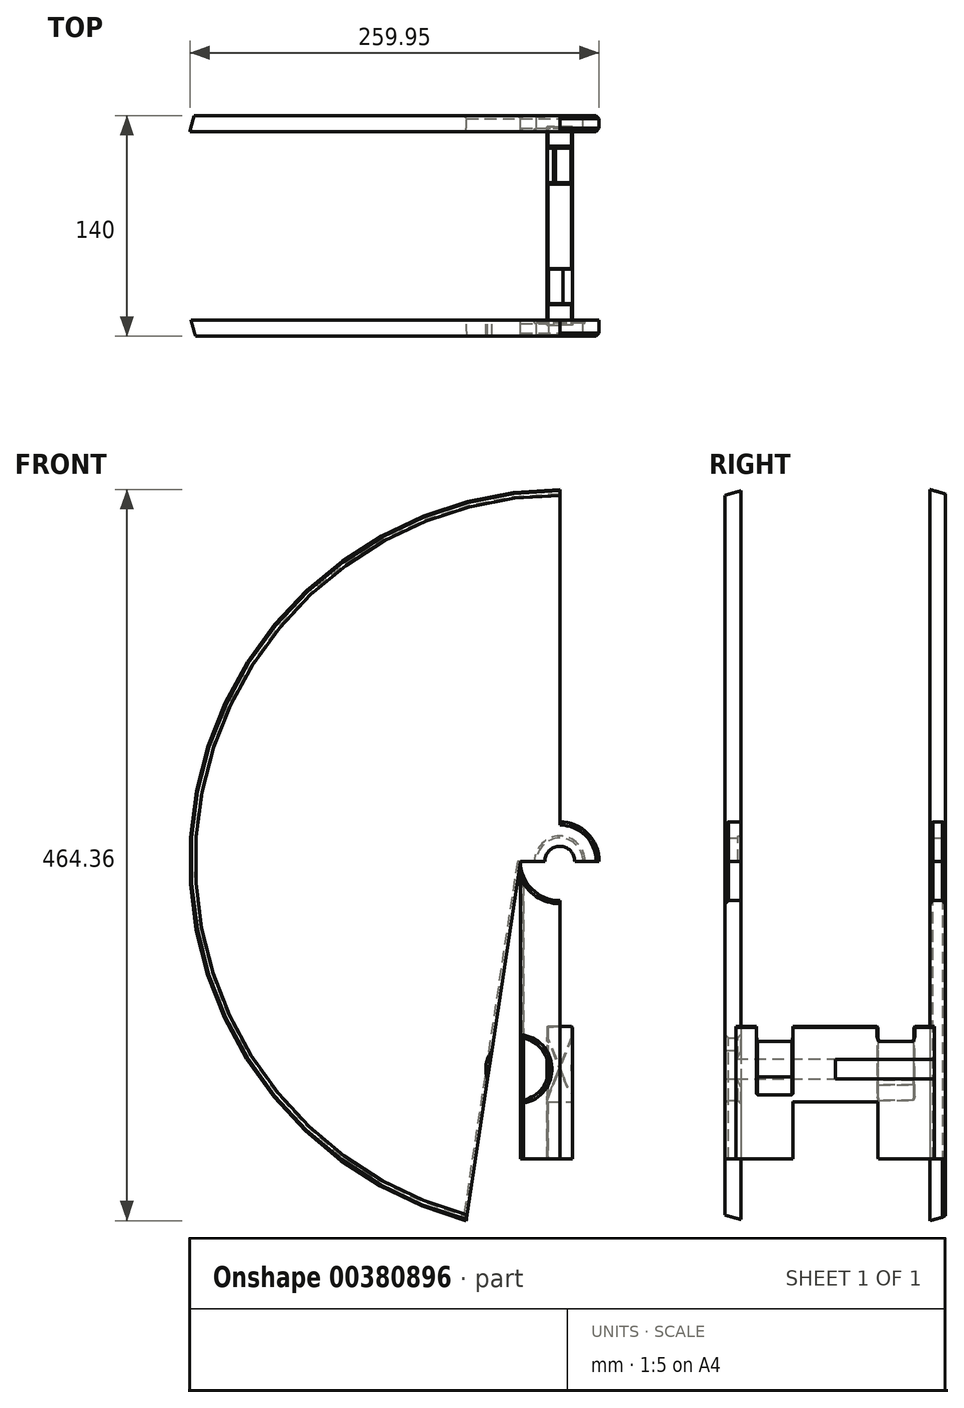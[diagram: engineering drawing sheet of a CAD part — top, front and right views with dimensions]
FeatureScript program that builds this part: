
annotation { "Feature Type Name" : "Feature", "Feature Type Description" : "" }
export const myFeature = defineFeature(function(context is Context, id is Id, definition is map)
    precondition{}
    {
        {
            var Q0;
            Q0=qCreatedBy(makeId("Right.planeOp"),FACE);
            var sketch = newSketch(context, id + "F0", { "sketchPlane" : qUnion([Q0])});
            skCircle(sketch, "E0", {"center": v(0, 0) * mm, "radius": 243.58 * mm});
            skLineSegment(sketch, "E1", {"start": v(1.44, 243.58) * mm, "end": v(1.44, -243.58) * mm});
            skCircle(sketch, "E2", {"center": v(0, 0) * mm, "radius": 251.5 * mm});
            skLineSegment(sketch, "E3", {"start": v(1.44, 243.58) * mm, "end": v(1.44, -357.35) * mm});
            skLineSegment(sketch, "E4", {"start": v(1.44, -357.35) * mm, "end": v(1.44, 517.62) * mm});
            skSolve(sketch);
        }
        {
            var Q0;
            Q0=qCreatedBy(makeId("Top.planeOp"),FACE);
            var sketch = newSketch(context, id + "F1", { "sketchPlane" : qUnion([Q0])});
            skCircle(sketch, "E5", {"center": v(0, 0) * mm, "radius": 243.58 * mm});
            skCircle(sketch, "E6", {"center": v(0, 0) * mm, "radius": 251.5 * mm});
            skSolve(sketch);
        }
        {
            var Q0;
            Q0=makeQuery(id+"F1.imprint","IMPRINT",FACE,{"disambiguationData":[TD([[makeQuery(id+"F1.imprint","IMPRINT",EDGE,{"derivedFrom":sQuery(id+"F1.wireOp",EDGE,"E5")}),1.0]])]});
            var sketch = newSketch(context, id + "F2", { "sketchPlane" : qUnion([Q0])});
            skCircle(sketch, "E7", {"center": v(0, 0) * mm, "radius": 50 * mm});
            skCircle(sketch, "E8", {"center": v(0, 0) * mm, "radius": 57.5 * mm});
            skSolve(sketch);
        }
        {
            var Q0;
            Q0=qCreatedBy(makeId("Front.planeOp"),FACE);
            var sketch = newSketch(context, id + "F3", { "sketchPlane" : qUnion([Q0])});
            skLineSegment(sketch, "E9.bottom", {"start": v(59.85, -25) * mm, "end": v(-59.85, -25) * mm});
            skLineSegment(sketch, "E9.top", {"start": v(59.85, 25) * mm, "end": v(-59.85, 25) * mm});
            skLineSegment(sketch, "E9.left", {"start": v(59.85, -25) * mm, "end": v(59.85, 25) * mm});
            skLineSegment(sketch, "E9.right", {"start": v(-59.85, -25) * mm, "end": v(-59.85, 25) * mm});
            skPoint(sketch, "E9.middle", {"position": v(0, 0) * mm});
            skCircle(sketch, "E10", {"center": v(0, 0) * mm, "radius": 14.75 * mm});
            skCircle(sketch, "E11", {"center": v(0, 0) * mm, "radius": 16 * mm});
            skCircle(sketch, "E12", {"center": v(0, 0) * mm, "radius": 9.5 * mm});
            skSolve(sketch);
        }
        {
            var Q0;
            Q0=qCreatedBy(makeId("Front.planeOp"),FACE);
            var sketch = newSketch(context, id + "F4", { "sketchPlane" : qUnion([Q0])});
            skCircle(sketch, "E13", {"center": v(0, 0) * mm, "radius": 25 * mm});
            skCircle(sketch, "E14", {"center": v(-1.44, -4.53) * mm, "radius": 243.58 * mm});
            skLineSegment(sketch, "E15", {"start": v(0, 239.04) * mm, "end": v(0, -248.1) * mm});
            skCircle(sketch, "E16", {"center": v(-1.44, -4.53) * mm, "radius": 251.5 * mm});
            skLineSegment(sketch, "E17", {"start": v(-25, 0) * mm, "end": v(-61.37, -240.62) * mm});
            skLineSegment(sketch, "E18.MirrorCS", {"start": v(25, 0) * mm, "end": v(61.37, -240.62) * mm});
            skLineSegment(sketch, "E19.bottom", {"start": v(-25, 0) * mm, "end": v(25, 0) * mm});
            skLineSegment(sketch, "E19.top", {"start": v(-25, -189.15) * mm, "end": v(25, -189.15) * mm});
            skLineSegment(sketch, "E19.left", {"start": v(-25, 0) * mm, "end": v(-25, -189.15) * mm});
            skLineSegment(sketch, "E19.right", {"start": v(25, 0) * mm, "end": v(25, -189.15) * mm});
            skSolve(sketch);
        }
        {
            var Q0;
            {var subQ0=sQuery(id+"F4.wireOp",EDGE,"E13");var subQ1=makeQuery(id+"F4.imprint","INTERSECT",VERTEX,{"derivedFrom":[subQ0,sQuery(id+"F4.wireOp",EDGE,"E17")]});Q0=makeQuery(id+"F4.imprint","IMPRINT",FACE,{"disambiguationData":[TD([[makeQuery(id+"F4.imprint","IMPRINT",EDGE,{"disambiguationData":[TD([[subQ1,1.0]])],"derivedFrom":subQ0}),1.0]])]});}
            var Q1;
            {var subQ0=sQuery(id+"F4.wireOp",EDGE,"E13");var subQ1=makeQuery(id+"F4.imprint","INTERSECT",VERTEX,{"derivedFrom":[subQ0,sQuery(id+"F4.wireOp",EDGE,"E18.MirrorCS")]});Q1=makeQuery(id+"F4.imprint","IMPRINT",FACE,{"disambiguationData":[TD([[makeQuery(id+"F4.imprint","IMPRINT",EDGE,{"disambiguationData":[TD([[subQ1,-1.0]])],"derivedFrom":subQ0}),1.0]])]});}
            var Q2;
            {var subQ0=sQuery(id+"F4.wireOp",EDGE,"E15");var subQ1=sQuery(id+"F4.wireOp",EDGE,"E13");var subQ2=makeQuery(id+"F4.imprint","INTERSECT",VERTEX,{"disambiguationData":[OD(1.0)],"derivedFrom":[subQ1,subQ0]});Q2=makeQuery(id+"F4.imprint","IMPRINT",FACE,{"disambiguationData":[TD([[makeQuery(id+"F4.imprint","IMPRINT",EDGE,{"disambiguationData":[TD([[subQ2,-1.0]])],"derivedFrom":subQ1}),-1.0]])]});}
            var Q3;
            {var subQ0=sQuery(id+"F4.wireOp",EDGE,"E19.left");Q3=makeQuery(id+"F4.imprint","IMPRINT",FACE,{"disambiguationData":[TD([[makeQuery(id+"F4.imprint","IMPRINT",EDGE,{"derivedFrom":subQ0}),1.0]])]});}
            var Q4;
            {var subQ0=sQuery(id+"F4.wireOp",EDGE,"E15");var subQ1=sQuery(id+"F4.wireOp",EDGE,"E13");var subQ2=makeQuery(id+"F4.imprint","INTERSECT",VERTEX,{"disambiguationData":[OD(1.0)],"derivedFrom":[subQ1,subQ0]});Q4=makeQuery(id+"F4.imprint","IMPRINT",FACE,{"disambiguationData":[TD([[makeQuery(id+"F4.imprint","IMPRINT",EDGE,{"disambiguationData":[TD([[subQ2,-1.0]])],"derivedFrom":subQ1}),1.0]])]});}
            var Q5;
            {var subQ1=sQuery(id+"F4.wireOp",EDGE,"E13");var subQ3=sQuery(id+"F4.wireOp",EDGE,"E15");var subQ4=makeQuery(id+"F4.imprint","INTERSECT",VERTEX,{"disambiguationData":[OD(1.0)],"derivedFrom":[subQ1,subQ3]});Q5=makeQuery(id+"F4.imprint","IMPRINT",FACE,{"disambiguationData":[TD([[makeQuery(id+"F4.imprint","IMPRINT",EDGE,{"disambiguationData":[TD([[subQ4,1.0]])],"derivedFrom":subQ3}),-1.0]])]});}
            extrude(context, id + "F5", {"entities" : qUnion([Q0, Q1, Q2, Q3, Q4, Q5]), "endBound" : BoundingType.SYMMETRIC, "depth" : 140 * mm, "hasSecondDirection" : true, "secondDirectionOppositeDirection" : true, "secondDirectionDepth" : 71 * mm});
        }
        {
            var Q0;
            {var subQ5=sQuery(id+"F4.wireOp",EDGE,"E13");var subQ6=makeQuery(id+"F4.imprint","INTERSECT",VERTEX,{"derivedFrom":[subQ5,sQuery(id+"F4.wireOp",EDGE,"E18.MirrorCS")]});Q0=makeQuery(id+"F4.imprint","IMPRINT",FACE,{"disambiguationData":[TD([[makeQuery(id+"F4.imprint","IMPRINT",EDGE,{"disambiguationData":[TD([[subQ6,-1.0]])],"derivedFrom":subQ5}),1.0]])]});}
            var Q1;
            {var subQ1=sQuery(id+"F4.wireOp",EDGE,"E13");var subQ3=sQuery(id+"F4.wireOp",EDGE,"E15");var subQ4=makeQuery(id+"F4.imprint","INTERSECT",VERTEX,{"disambiguationData":[OD(0.0)],"derivedFrom":[subQ1,subQ3]});Q1=makeQuery(id+"F4.imprint","IMPRINT",FACE,{"disambiguationData":[TD([[makeQuery(id+"F4.imprint","IMPRINT",EDGE,{"disambiguationData":[TD([[subQ4,-1.0]])],"derivedFrom":subQ3}),-1.0]])]});}
            var Q2;
            {var subQ1=sQuery(id+"F4.wireOp",EDGE,"E13");var subQ3=sQuery(id+"F4.wireOp",EDGE,"E15");var subQ4=makeQuery(id+"F4.imprint","INTERSECT",VERTEX,{"disambiguationData":[OD(1.0)],"derivedFrom":[subQ1,subQ3]});Q2=makeQuery(id+"F4.imprint","IMPRINT",FACE,{"disambiguationData":[TD([[makeQuery(id+"F4.imprint","IMPRINT",EDGE,{"disambiguationData":[TD([[subQ4,1.0]])],"derivedFrom":subQ3}),-1.0]])]});}
            var Q3;
            {var subQ0=sQuery(id+"F4.wireOp",EDGE,"E15");var subQ1=sQuery(id+"F4.wireOp",EDGE,"E13");var subQ2=makeQuery(id+"F4.imprint","INTERSECT",VERTEX,{"disambiguationData":[OD(1.0)],"derivedFrom":[subQ1,subQ0]});Q3=makeQuery(id+"F4.imprint","IMPRINT",FACE,{"disambiguationData":[TD([[makeQuery(id+"F4.imprint","IMPRINT",EDGE,{"disambiguationData":[TD([[subQ2,-1.0]])],"derivedFrom":subQ1}),1.0]])]});}
            var Q4;
            {var subQ0=sQuery(id+"F4.wireOp",EDGE,"E15");var subQ1=sQuery(id+"F4.wireOp",EDGE,"E13");var subQ2=makeQuery(id+"F4.imprint","INTERSECT",VERTEX,{"disambiguationData":[OD(1.0)],"derivedFrom":[subQ1,subQ0]});Q4=makeQuery(id+"F4.imprint","IMPRINT",FACE,{"disambiguationData":[TD([[makeQuery(id+"F4.imprint","IMPRINT",EDGE,{"disambiguationData":[TD([[subQ2,-1.0]])],"derivedFrom":subQ1}),-1.0]])]});}
            var Q5;
            {var subQ0=sQuery(id+"F4.wireOp",EDGE,"E19.left");Q5=makeQuery(id+"F4.imprint","IMPRINT",FACE,{"disambiguationData":[TD([[makeQuery(id+"F4.imprint","IMPRINT",EDGE,{"derivedFrom":subQ0}),1.0]])]});}
            extrude(context, id + "F6", {"entities" : qUnion([Q0, Q1, Q2, Q3, Q4, Q5]), "operationType" : NewBodyOperationType.REMOVE, "endBound" : BoundingType.SYMMETRIC, "oppositeDirection" : true, "depth" : 120 * mm});
        }
        {
            var Q0;
            {var subQ0=sQuery(id+"F0.wireOp",EDGE,"E4");var subQ1=sQuery(id+"F0.wireOp",EDGE,"E0");var subQ2=makeQuery(id+"F0.imprint","INTERSECT",VERTEX,{"disambiguationData":[OD(0.0)],"derivedFrom":[subQ1,subQ0]});Q0=makeQuery(id+"F0.imprint","IMPRINT",FACE,{"disambiguationData":[TD([[makeQuery(id+"F0.imprint","IMPRINT",EDGE,{"disambiguationData":[TD([[subQ2,1.0]])],"derivedFrom":subQ1}),1.0]])]});}
            var Q1;
            Q1=sQuery(id+"F0.wireOp",EDGE,"E4");
            revolve(context, id + "F7", {"operationType" : NewBodyOperationType.INTERSECT, "entities" : qUnion([Q0]), "axis" : qUnion([Q1]), "revolveType" : RevolveType.FULL});
        }
        {
            var Q0;
            Q0=makeQuery(id+"F3.imprint","IMPRINT",FACE,{"disambiguationData":[TD([[makeQuery(id+"F3.imprint","IMPRINT",EDGE,{"derivedFrom":sQuery(id+"F3.wireOp",EDGE,"E10")}),1.0]])]});
            var Q1;
            Q1=makeQuery(id+"F3.imprint","IMPRINT",FACE,{"disambiguationData":[TD([[makeQuery(id+"F3.imprint","IMPRINT",EDGE,{"derivedFrom":sQuery(id+"F3.wireOp",EDGE,"E10")}),-1.0]])]});
            var Q2;
            Q2=sQuery(id+"F4.wireOp",EDGE,"E13");
            extrude(context, id + "F8", {"entities" : qUnion([Q0, Q1]), "operationType" : NewBodyOperationType.REMOVE, "surfaceEntities" : qUnion([Q2]), "endBound" : BoundingType.SYMMETRIC, "depth" : 123.5 * mm});
        }
        {
            var Q0;
            Q0=makeQuery(id+"F3.imprint","IMPRINT",FACE,{"disambiguationData":[TD([[makeQuery(id+"F3.imprint","IMPRINT",EDGE,{"derivedFrom":sQuery(id+"F3.wireOp",EDGE,"E10")}),1.0]])]});
            extrude(context, id + "F9", {"entities" : qUnion([Q0]), "operationType" : NewBodyOperationType.REMOVE, "endBound" : BoundingType.SYMMETRIC, "depth" : 139 * mm});
        }
        {
            var Q0;
            Q0=qCreatedBy(makeId("Front.planeOp"),FACE);
            var sketch = newSketch(context, id + "F10", { "sketchPlane" : qUnion([Q0])});
            skLineSegment(sketch, "E20.bottom", {"start": v(-62.5, 105) * mm, "end": v(62.5, 105) * mm, "construction": true});
            skLineSegment(sketch, "E20.top", {"start": v(-62.5, -105) * mm, "end": v(62.5, -105) * mm, "construction": true});
            skLineSegment(sketch, "E20.left", {"start": v(-62.5, 105) * mm, "end": v(-62.5, -105) * mm, "construction": true});
            skLineSegment(sketch, "E20.right", {"start": v(62.5, 105) * mm, "end": v(62.5, -105) * mm, "construction": true});
            skPoint(sketch, "E20.middle", {"position": v(0, 0) * mm});
            skLineSegment(sketch, "E21", {"start": v(0, 0) * mm, "end": v(0, -232.3) * mm, "construction": true});
            skPoint(sketch, "E22.firstSnap0", {"position": v(0, -105) * mm});
            skLineSegment(sketch, "E22.bottom", {"start": v(0, -105) * mm, "end": v(-8.15, -105) * mm});
            skLineSegment(sketch, "E22.top", {"start": v(0, -232.3) * mm, "end": v(-8.15, -232.3) * mm});
            skLineSegment(sketch, "E22.left", {"start": v(0, -105) * mm, "end": v(0, -232.3) * mm});
            skLineSegment(sketch, "E22.right", {"start": v(-8.15, -105) * mm, "end": v(-8.15, -232.3) * mm});
            skLineSegment(sketch, "E23.bottom", {"start": v(0, -105) * mm, "end": v(8.15, -105) * mm});
            skLineSegment(sketch, "E23.top", {"start": v(0, -232.3) * mm, "end": v(8.15, -232.3) * mm});
            skLineSegment(sketch, "E23.right", {"start": v(8.15, -105) * mm, "end": v(8.15, -232.3) * mm});
            skSolve(sketch);
        }
        {
            var Q0;
            Q0=makeQuery(id+"F3.imprint","IMPRINT",FACE,{"disambiguationData":[TD([[makeQuery(id+"F3.imprint","IMPRINT",EDGE,{"derivedFrom":sQuery(id+"F3.wireOp",EDGE,"E12")}),1.0]])]});
            var Q1;
            Q1=sQuery(id+"F3.wireOp",EDGE,"E12");
            extrude(context, id + "F11", {"entities" : qUnion([Q0]), "operationType" : NewBodyOperationType.REMOVE, "surfaceEntities" : qUnion([Q1]), "endBound" : BoundingType.SYMMETRIC, "oppositeDirection" : true, "depth" : 200 * mm});
        }
        {
            var Q0;
            Q0=makeQuery(id+"F10.imprint","IMPRINT",FACE,{"disambiguationData":[TD([[makeQuery(id+"F10.imprint","IMPRINT",EDGE,{"derivedFrom":sQuery(id+"F10.wireOp",EDGE,"E23.bottom")}),-1.0]])]});
            var Q1;
            Q1=makeQuery(id+"F10.imprint","IMPRINT",FACE,{"disambiguationData":[TD([[makeQuery(id+"F10.imprint","IMPRINT",EDGE,{"derivedFrom":sQuery(id+"F10.wireOp",EDGE,"E22.bottom")}),1.0]])]});
            extrude(context, id + "F12", {"entities" : qUnion([Q0, Q1]), "operationType" : NewBodyOperationType.REMOVE, "endBound" : BoundingType.SYMMETRIC, "oppositeDirection" : true, "depth" : 126 * mm});
        }
        {
            var Q0;
            Q0=qCreatedBy(makeId("Front.planeOp"),FACE);
            var sketch = newSketch(context, id + "F13", { "sketchPlane" : qUnion([Q0])});
            skLineSegment(sketch, "E24.bottom", {"start": v(-62.5, 105) * mm, "end": v(62.5, 105) * mm, "construction": true});
            skLineSegment(sketch, "E24.top", {"start": v(-62.5, -105) * mm, "end": v(62.5, -105) * mm, "construction": true});
            skLineSegment(sketch, "E24.left", {"start": v(-62.5, 105) * mm, "end": v(-62.5, -105) * mm, "construction": true});
            skLineSegment(sketch, "E24.right", {"start": v(62.5, 105) * mm, "end": v(62.5, -105) * mm, "construction": true});
            skPoint(sketch, "E24.middle", {"position": v(0, 0) * mm});
            skLineSegment(sketch, "E25", {"start": v(0, 0) * mm, "end": v(0, -189) * mm, "construction": true});
            skPoint(sketch, "E26.firstSnap0", {"position": v(0, -105) * mm});
            skLineSegment(sketch, "E26.bottom", {"start": v(0, -105) * mm, "end": v(-8, -105) * mm});
            skLineSegment(sketch, "E26.top", {"start": v(0, -189) * mm, "end": v(-8, -189) * mm});
            skLineSegment(sketch, "E26.left", {"start": v(0, -105) * mm, "end": v(0, -189) * mm});
            skLineSegment(sketch, "E26.right", {"start": v(-8, -105) * mm, "end": v(-8, -189) * mm});
            skLineSegment(sketch, "E27.bottom", {"start": v(0, -105) * mm, "end": v(8, -105) * mm});
            skLineSegment(sketch, "E27.top", {"start": v(0, -189) * mm, "end": v(8, -189) * mm});
            skLineSegment(sketch, "E27.right", {"start": v(8, -105) * mm, "end": v(8, -189) * mm});
            skLineSegment(sketch, "E28", {"start": v(-63.01, -125.52) * mm, "end": v(62.14, -125.52) * mm, "construction": true});
            skLineSegment(sketch, "E29.bottom", {"start": v(-56.15, -105) * mm, "end": v(-48.17, -105) * mm});
            skSolve(sketch);
        }
        {
            var Q0;
            Q0=qCreatedBy(makeId("Front.planeOp"),FACE);
            var sketch = newSketch(context, id + "F14", { "sketchPlane" : qUnion([Q0])});
            skLineSegment(sketch, "E30", {"start": v(-75.64, -132) * mm, "end": v(82.36, -132) * mm, "construction": true});
            skCircle(sketch, "E31", {"center": v(-26.97, -132) * mm, "radius": 20 * mm});
            skCircle(sketch, "E32", {"center": v(27.03, -132) * mm, "radius": 20 * mm});
            skLineSegment(sketch, "E33", {"start": v(0, -132) * mm, "end": v(0, 0) * mm, "construction": true});
            skSolve(sketch);
        }
        {
            var Q0;
            Q0=makeQuery(id+"F13.imprint","IMPRINT",FACE,{"disambiguationData":[TD([[makeQuery(id+"F13.imprint","IMPRINT",EDGE,{"derivedFrom":sQuery(id+"F13.wireOp",EDGE,"E26.bottom")}),1.0]])]});
            var Q1;
            Q1=makeQuery(id+"F13.imprint","IMPRINT",FACE,{"disambiguationData":[TD([[makeQuery(id+"F13.imprint","IMPRINT",EDGE,{"derivedFrom":sQuery(id+"F13.wireOp",EDGE,"E27.bottom")}),-1.0]])]});
            extrude(context, id + "F15", {"entities" : qUnion([Q0, Q1]), "endBound" : BoundingType.SYMMETRIC, "depth" : 126 * mm});
        }
        {
            var Q0;
            Q0=makeQuery(id+"F14.imprint","IMPRINT",FACE,{"disambiguationData":[TD([[makeQuery(id+"F14.imprint","IMPRINT",EDGE,{"derivedFrom":sQuery(id+"F14.wireOp",EDGE,"E32")}),1.0]])]});
            extrude(context, id + "F16", {"entities" : qUnion([Q0]), "operationType" : NewBodyOperationType.REMOVE, "oppositeDirection" : true, "depth" : 125.4 * mm});
        }
        {
            var Q0;
            Q0=makeQuery(id+"F14.imprint","IMPRINT",FACE,{"disambiguationData":[TD([[makeQuery(id+"F14.imprint","IMPRINT",EDGE,{"derivedFrom":sQuery(id+"F14.wireOp",EDGE,"E31")}),1.0]])]});
            extrude(context, id + "F17", {"entities" : qUnion([Q0]), "operationType" : NewBodyOperationType.REMOVE, "depth" : 97.5 * mm});
        }
        {
            var Q0;
            Q0=qCreatedBy(makeId("Front.planeOp"),FACE);
            var sketch = newSketch(context, id + "F18", { "sketchPlane" : qUnion([Q0])});
            skCircle(sketch, "E34", {"center": v(0, 0) * mm, "radius": 242.5 * mm});
            skSolve(sketch);
        }
        {
            var Q0;
            Q0=makeQuery(id+"F14.imprint","IMPRINT",FACE,{"disambiguationData":[TD([[makeQuery(id+"F14.imprint","IMPRINT",EDGE,{"derivedFrom":sQuery(id+"F14.wireOp",EDGE,"E31")}),1.0]])]});
            extrude(context, id + "F19", {"entities" : qUnion([Q0]), "operationType" : NewBodyOperationType.REMOVE, "depth" : 159.82 * mm, "hasSecondDirection" : true, "secondDirectionOppositeDirection" : false, "secondDirectionDepth" : 5 * mm});
        }
        {
            var Q0;
            Q0=makeQuery(id+"F14.imprint","IMPRINT",FACE,{"disambiguationData":[TD([[makeQuery(id+"F14.imprint","IMPRINT",EDGE,{"derivedFrom":sQuery(id+"F14.wireOp",EDGE,"E32")}),1.0]])]});
            extrude(context, id + "F20", {"entities" : qUnion([Q0]), "operationType" : NewBodyOperationType.REMOVE, "oppositeDirection" : true, "depth" : 139.38 * mm, "hasSecondDirection" : true, "secondDirectionOppositeDirection" : true, "secondDirectionDepth" : 5 * mm});
        }
        {
            var Q0;
            Q0 = qSketchRegion(id + "F14", true);
            var sketch = newSketch(context, id + "F21", { "sketchPlane" : qUnion([Q0])});
            skLineSegment(sketch, "E35", {"start": v(-64.6, -131.33) * mm, "end": v(93.4, -131.33) * mm, "construction": true});
            skCircle(sketch, "E36", {"center": v(-26.64, -131.33) * mm, "radius": 25 * mm});
            skCircle(sketch, "E37", {"center": v(26.36, -131.33) * mm, "radius": 25 * mm});
            skLineSegment(sketch, "E38", {"start": v(0, -131.33) * mm, "end": v(0, 0.67) * mm, "construction": true});
            skSolve(sketch);
        }
        {
            var Q0;
            Q0 = qSketchRegion(id + "F21", true);
            var sketch = newSketch(context, id + "F22", { "sketchPlane" : qUnion([Q0])});
            skLineSegment(sketch, "E39.bottom", {"start": v(-20, -81.91) * mm, "end": v(20, -81.91) * mm});
            skLineSegment(sketch, "E39.top", {"start": v(-20, -181.91) * mm, "end": v(20, -181.91) * mm});
            skLineSegment(sketch, "E39.left", {"start": v(-20, -81.91) * mm, "end": v(-20, -181.91) * mm});
            skLineSegment(sketch, "E39.right", {"start": v(20, -81.91) * mm, "end": v(20, -181.91) * mm});
            skPoint(sketch, "E39.middle", {"position": v(0, -131.91) * mm});
            skLineSegment(sketch, "E40", {"start": v(20, -181.91) * mm, "end": v(-20, -81.91) * mm});
            skLineSegment(sketch, "E41", {"start": v(20, -81.91) * mm, "end": v(-20, -181.91) * mm});
            skSolve(sketch);
        }
        {
            var Q0;
            {var subQ0=sQuery(id+"F22.wireOp",EDGE,"E39.left");var subQ1=makeQuery(id+"F21.imprint","IMPRINT",EDGE,{"derivedFrom":sQuery(id+"F21.wireOp",EDGE,"E36")});var subQ2=makeQuery(id+"F22.imprint","INTERSECT",VERTEX,{"disambiguationData":[OD(0.0)],"derivedFrom":[subQ1,subQ0]});Q0=makeQuery(id+"F22.imprint","IMPRINT",FACE,{"disambiguationData":[TD([[makeQuery(id+"F22.imprint","IMPRINT",EDGE,{"disambiguationData":[TD([[subQ2,-1.0]])],"derivedFrom":subQ0}),-1.0]])]});}
            var Q1;
            Q1=makeQuery(id+"F21.imprint","IMPRINT",FACE,{"disambiguationData":[TD([[makeQuery(id+"F21.imprint","IMPRINT",EDGE,{"derivedFrom":sQuery(id+"F21.wireOp",EDGE,"E36")}),1.0]])]});
            var Q2;
            Q2=makeQuery(id+"F21.imprint","IMPRINT",FACE,{"disambiguationData":[TD([[makeQuery(id+"F21.imprint","IMPRINT",EDGE,{"derivedFrom":makeQuery(id+"F14.imprint","IMPRINT",EDGE,{"derivedFrom":sQuery(id+"F14.wireOp",EDGE,"E31")})}),1.0]])]});
            var Q3;
            {var subQ1=sQuery(id+"F22.wireOp",EDGE,"E39.left");var subQ3=makeQuery(id+"F21.imprint","IMPRINT",EDGE,{"derivedFrom":sQuery(id+"F21.wireOp",EDGE,"E36")});var subQ4=makeQuery(id+"F22.imprint","INTERSECT",VERTEX,{"disambiguationData":[OD(0.0)],"derivedFrom":[subQ3,subQ1]});Q3=makeQuery(id+"F22.imprint","IMPRINT",FACE,{"disambiguationData":[TD([[makeQuery(id+"F22.imprint","IMPRINT",EDGE,{"disambiguationData":[TD([[subQ4,1.0]])],"derivedFrom":subQ3}),-1.0]])]});}
            var Q4;
            {var subQ1=sQuery(id+"F22.wireOp",EDGE,"E39.bottom");Q4=makeQuery(id+"F22.imprint","IMPRINT",FACE,{"disambiguationData":[TD([[makeQuery(id+"F22.imprint","IMPRINT",EDGE,{"derivedFrom":subQ1}),-1.0]])]});}
            var Q5;
            {var subQ0=sQuery(id+"F22.wireOp",EDGE,"E41");var subQ1=sQuery(id+"F22.wireOp",EDGE,"E40");var subQ2=makeQuery(id+"F22.imprint","INTERSECT",VERTEX,{"derivedFrom":[subQ1,subQ0]});Q5=makeQuery(id+"F22.imprint","IMPRINT",FACE,{"disambiguationData":[TD([[makeQuery(id+"F22.imprint","IMPRINT",EDGE,{"disambiguationData":[TD([[subQ2,-1.0]])],"derivedFrom":subQ1}),1.0]])]});}
            var Q6;
            {var subQ0=sQuery(id+"F22.wireOp",EDGE,"E41");var subQ1=makeQuery(id+"F21.imprint","IMPRINT",EDGE,{"derivedFrom":sQuery(id+"F21.wireOp",EDGE,"E37")});var subQ2=makeQuery(id+"F22.imprint","INTERSECT",VERTEX,{"disambiguationData":[OD(0.0)],"derivedFrom":[subQ1,subQ0]});Q6=makeQuery(id+"F22.imprint","IMPRINT",FACE,{"disambiguationData":[TD([[makeQuery(id+"F22.imprint","IMPRINT",EDGE,{"disambiguationData":[TD([[subQ2,-1.0]])],"derivedFrom":subQ0}),-1.0]])]});}
            extrude(context, id + "F23", {"entities" : qUnion([Q0, Q1, Q2, Q3, Q4, Q5, Q6]), "operationType" : NewBodyOperationType.REMOVE, "oppositeDirection" : true, "depth" : 50 * mm, "hasSecondDirection" : true, "secondDirectionOppositeDirection" : true, "secondDirectionDepth" : 27 * mm});
        }
        {
            var Q0;
            {var subQ0=sQuery(id+"F22.wireOp",EDGE,"E39.right");var subQ1=makeQuery(id+"F21.imprint","IMPRINT",EDGE,{"derivedFrom":makeQuery(id+"F14.imprint","IMPRINT",EDGE,{"derivedFrom":sQuery(id+"F14.wireOp",EDGE,"E32")})});var subQ2=makeQuery(id+"F22.imprint","INTERSECT",VERTEX,{"disambiguationData":[OD(0.0)],"derivedFrom":[subQ1,subQ0]});Q0=makeQuery(id+"F22.imprint","IMPRINT",FACE,{"disambiguationData":[TD([[makeQuery(id+"F22.imprint","IMPRINT",EDGE,{"disambiguationData":[TD([[subQ2,-1.0]])],"derivedFrom":subQ0}),-1.0]])]});}
            var Q1;
            {var subQ1=makeQuery(id+"F21.imprint","IMPRINT",EDGE,{"derivedFrom":sQuery(id+"F21.wireOp",EDGE,"E37")});var subQ4=sQuery(id+"F22.wireOp",EDGE,"E39.right");var subQ5=makeQuery(id+"F22.imprint","INTERSECT",VERTEX,{"disambiguationData":[OD(0.0)],"derivedFrom":[subQ1,subQ4]});Q1=makeQuery(id+"F22.imprint","IMPRINT",FACE,{"disambiguationData":[TD([[makeQuery(id+"F22.imprint","IMPRINT",EDGE,{"disambiguationData":[TD([[subQ5,-1.0]])],"derivedFrom":subQ4}),-1.0]])]});}
            var Q2;
            Q2=makeQuery(id+"F21.imprint","IMPRINT",FACE,{"disambiguationData":[TD([[makeQuery(id+"F21.imprint","IMPRINT",EDGE,{"derivedFrom":makeQuery(id+"F14.imprint","IMPRINT",EDGE,{"derivedFrom":sQuery(id+"F14.wireOp",EDGE,"E32")})}),1.0]])]});
            var Q3;
            {var subQ0=sQuery(id+"F22.wireOp",EDGE,"E41");var subQ1=sQuery(id+"F22.wireOp",EDGE,"E40");var subQ2=makeQuery(id+"F22.imprint","INTERSECT",VERTEX,{"derivedFrom":[subQ1,subQ0]});Q3=makeQuery(id+"F22.imprint","IMPRINT",FACE,{"disambiguationData":[TD([[makeQuery(id+"F22.imprint","IMPRINT",EDGE,{"disambiguationData":[TD([[subQ2,1.0]])],"derivedFrom":subQ1}),-1.0]])]});}
            var Q4;
            {var subQ1=sQuery(id+"F22.wireOp",EDGE,"E39.right");var subQ3=makeQuery(id+"F21.imprint","IMPRINT",EDGE,{"derivedFrom":sQuery(id+"F21.wireOp",EDGE,"E37")});var subQ4=makeQuery(id+"F22.imprint","INTERSECT",VERTEX,{"disambiguationData":[OD(0.0)],"derivedFrom":[subQ3,subQ1]});Q4=makeQuery(id+"F22.imprint","IMPRINT",FACE,{"disambiguationData":[TD([[makeQuery(id+"F22.imprint","IMPRINT",EDGE,{"disambiguationData":[TD([[subQ4,-1.0]])],"derivedFrom":subQ3}),-1.0]])]});}
            var Q5;
            {var subQ1=sQuery(id+"F22.wireOp",EDGE,"E39.bottom");Q5=makeQuery(id+"F22.imprint","IMPRINT",FACE,{"disambiguationData":[TD([[makeQuery(id+"F22.imprint","IMPRINT",EDGE,{"derivedFrom":subQ1}),-1.0]])]});}
            var Q6;
            Q6=makeQuery(id+"F21.imprint","IMPRINT",FACE,{"disambiguationData":[TD([[makeQuery(id+"F21.imprint","IMPRINT",EDGE,{"derivedFrom":sQuery(id+"F21.wireOp",EDGE,"E37")}),1.0]])]});
            var Q7;
            {var subQ0=sQuery(id+"F22.wireOp",EDGE,"E40");var subQ1=makeQuery(id+"F21.imprint","IMPRINT",EDGE,{"derivedFrom":sQuery(id+"F21.wireOp",EDGE,"E36")});var subQ2=makeQuery(id+"F22.imprint","INTERSECT",VERTEX,{"disambiguationData":[OD(0.0)],"derivedFrom":[subQ1,subQ0]});Q7=makeQuery(id+"F22.imprint","IMPRINT",FACE,{"disambiguationData":[TD([[makeQuery(id+"F22.imprint","IMPRINT",EDGE,{"disambiguationData":[TD([[subQ2,-1.0]])],"derivedFrom":subQ0}),-1.0]])]});}
            extrude(context, id + "F24", {"entities" : qUnion([Q0, Q1, Q2, Q3, Q4, Q5, Q6, Q7]), "operationType" : NewBodyOperationType.REMOVE, "depth" : 50 * mm, "hasSecondDirection" : true, "secondDirectionOppositeDirection" : false, "secondDirectionDepth" : 27 * mm});
        }
        {
            var Q0;
            Q0=makeQuery(id+"F5.opExtrude","CAP_EDGE",EDGE,{"disambiguationData":[OSD([sQuery(id+"F4.wireOp",EDGE,"E17")])],"isStart":true});
            var Q1;
            Q1=makeQuery(id+"F5.opExtrude","CAP_EDGE",EDGE,{"disambiguationData":[OSD([sQuery(id+"F4.wireOp",EDGE,"E18.MirrorCS")])],"isStart":true});
            var Q2;
            Q2=makeQuery(id+"F5.opExtrude","CAP_EDGE",EDGE,{"disambiguationData":[OSD([sQuery(id+"F4.wireOp",EDGE,"E19.right")])],"isStart":false});
            var Q3;
            Q3=makeQuery(id+"F5.opExtrude","CAP_EDGE",EDGE,{"disambiguationData":[OSD([sQuery(id+"F4.wireOp",EDGE,"E13")])],"isStart":false});
            var Q4;
            Q4=makeQuery(id+"F5.opExtrude","CAP_EDGE",EDGE,{"disambiguationData":[OSD([sQuery(id+"F4.wireOp",EDGE,"E13")])],"isStart":true});
            var Q5;
            Q5=makeQuery(id+"F5.opExtrude","CAP_EDGE",EDGE,{"disambiguationData":[OSD([sQuery(id+"F4.wireOp",EDGE,"E19.left")])],"isStart":true});
            var Q6;
            Q6=makeQuery(id+"F5.opExtrude","CAP_EDGE",EDGE,{"disambiguationData":[OSD([sQuery(id+"F4.wireOp",EDGE,"E19.right")])],"isStart":true});
            var Q7;
            Q7=makeQuery(id+"F17.boolean.opBoolean","INTERSECT",EDGE,{"derivedFrom":[makeQuery(id+"F5.opExtrude","CAP_FACE",FACE,{"disambiguationData":[OSD([sQuery(id+"F4.wireOp",EDGE,"E13"),sQuery(id+"F4.wireOp",EDGE,"E19.top"),sQuery(id+"F4.wireOp",EDGE,"E19.left"),sQuery(id+"F4.wireOp",EDGE,"E19.right")])],"isStart":false}),makeQuery(id+"F17.opExtrude","SWEPT_FACE",FACE,{"disambiguationData":[OSD([sQuery(id+"F14.wireOp",EDGE,"E31")])]})]});
            var Q8;
            Q8=makeQuery(id+"F16.boolean.opBoolean","INTERSECT",EDGE,{"derivedFrom":[makeQuery(id+"F5.opExtrude","CAP_FACE",FACE,{"disambiguationData":[OSD([sQuery(id+"F4.wireOp",EDGE,"E13"),sQuery(id+"F4.wireOp",EDGE,"E19.top"),sQuery(id+"F4.wireOp",EDGE,"E19.left"),sQuery(id+"F4.wireOp",EDGE,"E19.right")])],"isStart":true}),makeQuery(id+"F16.opExtrude","SWEPT_FACE",FACE,{"disambiguationData":[OSD([sQuery(id+"F14.wireOp",EDGE,"E32")])]})]});
            var Q9;
            {var subQ0=sQuery(id+"F4.wireOp",EDGE,"E19.left");var subQ1=sQuery(id+"F4.wireOp",EDGE,"E19.top");Q9=makeQuery(id+"F17.boolean.opBoolean","SPLIT",EDGE,{"disambiguationData":[TD([makeQuery(id+"F5.opExtrude","SWEPT_FACE",FACE,{"disambiguationData":[OSD([subQ1])]})])],"derivedFrom":makeQuery(id+"F5.opExtrude","CAP_EDGE",EDGE,{"disambiguationData":[OSD([subQ0])],"isStart":false})});}
            var Q10;
            Q10=makeQuery(id+"F6.boolean.opBoolean","COPY",EDGE,{"derivedFrom":makeQuery(id+"F6.opExtrude","CAP_EDGE",EDGE,{"disambiguationData":[OSD([sQuery(id+"F4.wireOp",EDGE,"E19.right")])],"isStart":true})});
            var Q11;
            Q11=makeQuery(id+"F6.boolean.opBoolean","COPY",EDGE,{"derivedFrom":makeQuery(id+"F6.opExtrude","CAP_EDGE",EDGE,{"disambiguationData":[OSD([sQuery(id+"F4.wireOp",EDGE,"E13")])],"isStart":true})});
            var Q12;
            Q12=makeQuery(id+"F6.boolean.opBoolean","COPY",EDGE,{"derivedFrom":makeQuery(id+"F6.opExtrude","CAP_EDGE",EDGE,{"disambiguationData":[OSD([sQuery(id+"F4.wireOp",EDGE,"E19.left")])],"isStart":false})});
            var Q13;
            Q13=makeQuery(id+"F6.boolean.opBoolean","COPY",EDGE,{"derivedFrom":makeQuery(id+"F6.opExtrude","CAP_EDGE",EDGE,{"disambiguationData":[OSD([sQuery(id+"F4.wireOp",EDGE,"E13")])],"isStart":false})});
            var Q14;
            {var subQ0=sQuery(id+"F4.wireOp",EDGE,"E13");var subQ1=sQuery(id+"F4.wireOp",EDGE,"E19.right");Q14=makeQuery(id+"F16.boolean.opBoolean","SPLIT",EDGE,{"disambiguationData":[TD([makeQuery(id+"F5.opExtrude","SWEPT_FACE",FACE,{"disambiguationData":[OSD([subQ0])]})])],"derivedFrom":makeQuery(id+"F6.boolean.opBoolean","COPY",EDGE,{"derivedFrom":makeQuery(id+"F6.opExtrude","CAP_EDGE",EDGE,{"disambiguationData":[OSD([subQ1])],"isStart":false})})});}
            var Q15;
            {var subQ0=sQuery(id+"F4.wireOp",EDGE,"E19.top");var subQ1=sQuery(id+"F4.wireOp",EDGE,"E19.right");Q15=makeQuery(id+"F16.boolean.opBoolean","SPLIT",EDGE,{"disambiguationData":[TD([makeQuery(id+"F5.opExtrude","SWEPT_FACE",FACE,{"disambiguationData":[OSD([subQ0])]})])],"derivedFrom":makeQuery(id+"F6.boolean.opBoolean","COPY",EDGE,{"derivedFrom":makeQuery(id+"F6.opExtrude","CAP_EDGE",EDGE,{"disambiguationData":[OSD([subQ1])],"isStart":false})})});}
            var Q16;
            {var subQ0=sQuery(id+"F4.wireOp",EDGE,"E19.left");var subQ1=sQuery(id+"F4.wireOp",EDGE,"E19.top");var subQ2=sQuery(id+"F4.wireOp",EDGE,"E19.right");var subQ3=sQuery(id+"F4.wireOp",EDGE,"E13");Q16=makeQuery(id+"F16.boolean.opBoolean","INTERSECT",EDGE,{"disambiguationData":[OD(1.0)],"derivedFrom":[makeQuery(id+"F8.boolean.opBoolean","SPLIT",FACE,{"disambiguationData":[TD([makeQuery(id+"F5.opExtrude","SWEPT_FACE",FACE,{"disambiguationData":[OSD([subQ3])]})])],"derivedFrom":makeQuery(id+"F6.boolean.opBoolean","COPY",FACE,{"derivedFrom":makeQuery(id+"F6.opExtrude","CAP_FACE",FACE,{"disambiguationData":[OSD([subQ3,subQ1,subQ0,subQ2])],"isStart":false})})}),makeQuery(id+"F16.opExtrude","SWEPT_FACE",FACE,{"disambiguationData":[OSD([sQuery(id+"F14.wireOp",EDGE,"E32")])]})]});}
            var Q17;
            {var subQ0=sQuery(id+"F4.wireOp",EDGE,"E19.left");var subQ1=sQuery(id+"F4.wireOp",EDGE,"E19.top");var subQ2=sQuery(id+"F4.wireOp",EDGE,"E19.right");var subQ3=sQuery(id+"F4.wireOp",EDGE,"E13");Q17=makeQuery(id+"F16.boolean.opBoolean","INTERSECT",EDGE,{"disambiguationData":[OD(0.0)],"derivedFrom":[makeQuery(id+"F8.boolean.opBoolean","SPLIT",FACE,{"disambiguationData":[TD([makeQuery(id+"F5.opExtrude","SWEPT_FACE",FACE,{"disambiguationData":[OSD([subQ3])]})])],"derivedFrom":makeQuery(id+"F6.boolean.opBoolean","COPY",FACE,{"derivedFrom":makeQuery(id+"F6.opExtrude","CAP_FACE",FACE,{"disambiguationData":[OSD([subQ3,subQ1,subQ0,subQ2])],"isStart":false})})}),makeQuery(id+"F16.opExtrude","SWEPT_FACE",FACE,{"disambiguationData":[OSD([sQuery(id+"F14.wireOp",EDGE,"E32")])]})]});}
            var Q18;
            Q18=makeQuery(id+"F16.boolean.opBoolean","INTERSECT",EDGE,{"derivedFrom":[makeQuery(id+"F12.boolean.opBoolean","COPY",FACE,{"derivedFrom":makeQuery(id+"F12.opExtrude","CAP_FACE",FACE,{"disambiguationData":[OSD([sQuery(id+"F10.wireOp",EDGE,"E22.bottom"),sQuery(id+"F10.wireOp",EDGE,"E22.top"),sQuery(id+"F10.wireOp",EDGE,"E22.right"),sQuery(id+"F10.wireOp",EDGE,"E23.bottom"),sQuery(id+"F10.wireOp",EDGE,"E23.top"),sQuery(id+"F10.wireOp",EDGE,"E23.right")])],"isStart":false})}),makeQuery(id+"F16.opExtrude","SWEPT_FACE",FACE,{"disambiguationData":[OSD([sQuery(id+"F14.wireOp",EDGE,"E32")])]})]});
            var Q19;
            Q19=makeQuery(id+"F20.boolean.opBoolean","INTERSECT",EDGE,{"derivedFrom":[makeQuery(id+"F15.opExtrude","SWEPT_FACE",FACE,{"disambiguationData":[OSD([sQuery(id+"F13.wireOp",EDGE,"E27.right")])]}),makeQuery(id+"F20.opExtrude","CAP_FACE",FACE,{"disambiguationData":[OSD([sQuery(id+"F14.wireOp",EDGE,"E32")])],"isStart":true})]});
            var Q20;
            Q20=makeQuery(id+"F19.boolean.opBoolean","COPY",EDGE,{"derivedFrom":makeQuery(id+"F19.opExtrude","CAP_EDGE",EDGE,{"disambiguationData":[OSD([sQuery(id+"F14.wireOp",EDGE,"E31")])],"isStart":true})});
            var Q21;
            Q21=makeQuery(id+"F19.boolean.opBoolean","INTERSECT",EDGE,{"derivedFrom":[makeQuery(id+"F15.opExtrude","CAP_FACE",FACE,{"disambiguationData":[OSD([sQuery(id+"F13.wireOp",EDGE,"E26.bottom"),sQuery(id+"F13.wireOp",EDGE,"E26.top"),sQuery(id+"F13.wireOp",EDGE,"E26.right"),sQuery(id+"F13.wireOp",EDGE,"E27.bottom"),sQuery(id+"F13.wireOp",EDGE,"E27.top"),sQuery(id+"F13.wireOp",EDGE,"E27.right")])],"isStart":false}),makeQuery(id+"F19.opExtrude","SWEPT_FACE",FACE,{"disambiguationData":[OSD([sQuery(id+"F14.wireOp",EDGE,"E31")])]})]});
            var Q22;
            {var subQ0=sQuery(id+"F4.wireOp",EDGE,"E19.left");var subQ1=sQuery(id+"F4.wireOp",EDGE,"E19.top");var subQ2=sQuery(id+"F4.wireOp",EDGE,"E19.right");var subQ3=sQuery(id+"F4.wireOp",EDGE,"E13");Q22=makeQuery(id+"F17.boolean.opBoolean","INTERSECT",EDGE,{"disambiguationData":[OD(1.0)],"derivedFrom":[makeQuery(id+"F8.boolean.opBoolean","SPLIT",FACE,{"disambiguationData":[TD([makeQuery(id+"F5.opExtrude","SWEPT_FACE",FACE,{"disambiguationData":[OSD([subQ3])]})])],"derivedFrom":makeQuery(id+"F6.boolean.opBoolean","COPY",FACE,{"derivedFrom":makeQuery(id+"F6.opExtrude","CAP_FACE",FACE,{"disambiguationData":[OSD([subQ3,subQ1,subQ0,subQ2])],"isStart":true})})}),makeQuery(id+"F17.opExtrude","SWEPT_FACE",FACE,{"disambiguationData":[OSD([sQuery(id+"F14.wireOp",EDGE,"E31")])]})]});}
            var Q23;
            {var subQ0=sQuery(id+"F4.wireOp",EDGE,"E19.left");var subQ1=sQuery(id+"F4.wireOp",EDGE,"E19.top");var subQ2=sQuery(id+"F4.wireOp",EDGE,"E19.right");var subQ3=sQuery(id+"F4.wireOp",EDGE,"E13");Q23=makeQuery(id+"F17.boolean.opBoolean","INTERSECT",EDGE,{"disambiguationData":[OD(0.0)],"derivedFrom":[makeQuery(id+"F8.boolean.opBoolean","SPLIT",FACE,{"disambiguationData":[TD([makeQuery(id+"F5.opExtrude","SWEPT_FACE",FACE,{"disambiguationData":[OSD([subQ3])]})])],"derivedFrom":makeQuery(id+"F6.boolean.opBoolean","COPY",FACE,{"derivedFrom":makeQuery(id+"F6.opExtrude","CAP_FACE",FACE,{"disambiguationData":[OSD([subQ3,subQ1,subQ0,subQ2])],"isStart":true})})}),makeQuery(id+"F17.opExtrude","SWEPT_FACE",FACE,{"disambiguationData":[OSD([sQuery(id+"F14.wireOp",EDGE,"E31")])]})]});}
            var Q24;
            {var subQ0=sQuery(id+"F4.wireOp",EDGE,"E19.top");var subQ1=sQuery(id+"F4.wireOp",EDGE,"E19.left");Q24=makeQuery(id+"F17.boolean.opBoolean","SPLIT",EDGE,{"disambiguationData":[TD([makeQuery(id+"F5.opExtrude","SWEPT_FACE",FACE,{"disambiguationData":[OSD([subQ0])]})])],"derivedFrom":makeQuery(id+"F6.boolean.opBoolean","COPY",EDGE,{"derivedFrom":makeQuery(id+"F6.opExtrude","CAP_EDGE",EDGE,{"disambiguationData":[OSD([subQ1])],"isStart":true})})});}
            chamfer(context, id + "F25", {"entities" : qUnion([Q0, Q1, Q2, Q3, Q4, Q5, Q6, Q7, Q8, Q9, Q10, Q11, Q12, Q13, Q14, Q15, Q16, Q17, Q18, Q19, Q20, Q21, Q22, Q23, Q24]), "width" : 2 * mm, "tangentPropagation" : true});
        }
        {
            var Q0;
            Q0=makeQuery(id+"F15.opExtrude","SWEPT_FACE",FACE,{"disambiguationData":[OSD([sQuery(id+"F13.wireOp",EDGE,"E27.right")])]});
            var sketch = newSketch(context, id + "F26", { "sketchPlane" : qUnion([Q0])});
            skLineSegment(sketch, "E42.bottom", {"start": v(27, -153) * mm, "end": v(-27, -153) * mm});
            skLineSegment(sketch, "E42.top", {"start": v(27, -225) * mm, "end": v(-27, -225) * mm});
            skLineSegment(sketch, "E42.left", {"start": v(27, -153) * mm, "end": v(27, -225) * mm});
            skLineSegment(sketch, "E42.right", {"start": v(-27, -153) * mm, "end": v(-27, -225) * mm});
            skPoint(sketch, "E42.middle", {"position": v(0, -189) * mm});
            skSolve(sketch);
        }
        {
            var Q0;
            Q0 = qSketchRegion(id + "F26", true);
            extrude(context, id + "F27", {"entities" : qUnion([Q0]), "operationType" : NewBodyOperationType.REMOVE, "oppositeDirection" : true, "depth" : 25 * mm});
        }
        {
            var Q0;
            Q0=makeQuery(id+"F15.opExtrude","SWEPT_EDGE",EDGE,{"disambiguationData":[OSD([sQuery(id+"F13.wireOp",EDGE,"E26.bottom"),sQuery(id+"F13.wireOp",EDGE,"E26.right")])]});
            var Q1;
            Q1=makeQuery(id+"F15.opExtrude","SWEPT_EDGE",EDGE,{"disambiguationData":[OSD([sQuery(id+"F13.wireOp",EDGE,"E27.bottom"),sQuery(id+"F13.wireOp",EDGE,"E27.right")])]});
            var Q2;
            Q2=makeQuery(id+"F23.boolean.opBoolean","COPY",EDGE,{"derivedFrom":makeQuery(id+"F23.opExtrude","SWEPT_EDGE",EDGE,{"disambiguationData":[OSD([sQuery(id+"F21.wireOp",EDGE,"E36"),sQuery(id+"F22.wireOp",EDGE,"E41")])]})});
            var Q3;
            Q3=makeQuery(id+"F23.boolean.opBoolean","INTERSECT",EDGE,{"derivedFrom":[makeQuery(id+"F15.opExtrude","SWEPT_FACE",FACE,{"disambiguationData":[OSD([sQuery(id+"F13.wireOp",EDGE,"E26.right")])]}),makeQuery(id+"F23.opExtrude","SWEPT_FACE",FACE,{"disambiguationData":[OSD([sQuery(id+"F21.wireOp",EDGE,"E36")])]})]});
            var Q4;
            Q4=makeQuery(id+"F23.boolean.opBoolean","INTERSECT",EDGE,{"derivedFrom":[makeQuery(id+"F15.opExtrude","SWEPT_FACE",FACE,{"disambiguationData":[OSD([sQuery(id+"F13.wireOp",EDGE,"E26.right")])]}),makeQuery(id+"F23.opExtrude","CAP_FACE",FACE,{"disambiguationData":[OSD([sQuery(id+"F21.wireOp",EDGE,"E36"),sQuery(id+"F22.wireOp",EDGE,"E39.bottom"),sQuery(id+"F22.wireOp",EDGE,"E39.left"),sQuery(id+"F22.wireOp",EDGE,"E41")])],"isStart":true})]});
            var Q5;
            Q5=makeQuery(id+"F23.boolean.opBoolean","COPY",FACE,{"derivedFrom":makeQuery(id+"F23.opExtrude","SWEPT_FACE",FACE,{"disambiguationData":[OSD([sQuery(id+"F22.wireOp",EDGE,"E41")])]})});
            var Q6;
            Q6=makeQuery(id+"F23.boolean.opBoolean","INTERSECT",EDGE,{"derivedFrom":[makeQuery(id+"F15.opExtrude","SWEPT_FACE",FACE,{"disambiguationData":[OSD([sQuery(id+"F13.wireOp",EDGE,"E26.bottom"),sQuery(id+"F13.wireOp",EDGE,"E27.bottom")])]}),makeQuery(id+"F23.opExtrude","CAP_FACE",FACE,{"disambiguationData":[OSD([sQuery(id+"F21.wireOp",EDGE,"E36"),sQuery(id+"F22.wireOp",EDGE,"E39.bottom"),sQuery(id+"F22.wireOp",EDGE,"E39.left"),sQuery(id+"F22.wireOp",EDGE,"E41")])],"isStart":false})]});
            var Q7;
            Q7=makeQuery(id+"F23.boolean.opBoolean","INTERSECT",EDGE,{"derivedFrom":[makeQuery(id+"F15.opExtrude","SWEPT_FACE",FACE,{"disambiguationData":[OSD([sQuery(id+"F13.wireOp",EDGE,"E26.bottom"),sQuery(id+"F13.wireOp",EDGE,"E27.bottom")])]}),makeQuery(id+"F23.opExtrude","CAP_FACE",FACE,{"disambiguationData":[OSD([sQuery(id+"F21.wireOp",EDGE,"E36"),sQuery(id+"F22.wireOp",EDGE,"E39.bottom"),sQuery(id+"F22.wireOp",EDGE,"E39.left"),sQuery(id+"F22.wireOp",EDGE,"E41")])],"isStart":true})]});
            var Q8;
            Q8=makeQuery(id+"F23.boolean.opBoolean","COPY",FACE,{"derivedFrom":makeQuery(id+"F23.opExtrude","SWEPT_FACE",FACE,{"disambiguationData":[OSD([sQuery(id+"F21.wireOp",EDGE,"E36")])]})});
            var Q9;
            Q9=makeQuery(id+"F24.boolean.opBoolean","COPY",FACE,{"derivedFrom":makeQuery(id+"F24.opExtrude","SWEPT_FACE",FACE,{"disambiguationData":[OSD([sQuery(id+"F22.wireOp",EDGE,"E40")])]})});
            var Q10;
            {var subQ0=sQuery(id+"F21.wireOp",EDGE,"E37");var subQ1=makeQuery(id+"F21.imprint","IMPRINT",EDGE,{"derivedFrom":subQ0});Q10=makeQuery(id+"F24.boolean.opBoolean","TWEAK_FACE",FACE,{"derivedFrom":[makeQuery(id+"F24.opExtrude","SWEPT_FACE",FACE,{"disambiguationData":[OSD([subQ0]),TDD([subQ1])]}),makeQuery(id+"F24.opExtrude","SWEPT_FACE",FACE,{"disambiguationData":[OSD([subQ0]),TDD([makeQuery(id+"F22.imprint","IMPRINT",EDGE,{"disambiguationData":[TD([[makeQuery(id+"F22.imprint","INTERSECT",VERTEX,{"disambiguationData":[OD(1.0)],"derivedFrom":[subQ1,sQuery(id+"F22.wireOp",EDGE,"E39.right")]}),1.0]])],"derivedFrom":subQ1})])]})]});}
            var Q11;
            {var subQ0=sQuery(id+"F21.wireOp",EDGE,"E37");Q11=makeQuery(id+"F24.boolean.opBoolean","TWEAK_FACE",FACE,{"derivedFrom":[makeQuery(id+"F24.opExtrude","CAP_FACE",FACE,{"disambiguationData":[OSD([subQ0])],"isStart":false}),makeQuery(id+"F24.opExtrude","CAP_FACE",FACE,{"disambiguationData":[OSD([subQ0,sQuery(id+"F22.wireOp",EDGE,"E39.bottom"),sQuery(id+"F22.wireOp",EDGE,"E39.right"),sQuery(id+"F22.wireOp",EDGE,"E40"),sQuery(id+"F22.wireOp",EDGE,"E41")])],"isStart":false})]});}
            var Q12;
            {var subQ0=sQuery(id+"F21.wireOp",EDGE,"E37");Q12=makeQuery(id+"F24.boolean.opBoolean","TWEAK_FACE",FACE,{"derivedFrom":[makeQuery(id+"F24.opExtrude","CAP_FACE",FACE,{"disambiguationData":[OSD([subQ0])],"isStart":true}),makeQuery(id+"F24.opExtrude","CAP_FACE",FACE,{"disambiguationData":[OSD([subQ0,sQuery(id+"F22.wireOp",EDGE,"E39.bottom"),sQuery(id+"F22.wireOp",EDGE,"E39.right"),sQuery(id+"F22.wireOp",EDGE,"E40"),sQuery(id+"F22.wireOp",EDGE,"E41")])],"isStart":true})]});}
            var Q13;
            Q13=makeQuery(id+"F27.boolean.opBoolean","INTERSECT",EDGE,{"derivedFrom":[makeQuery(id+"F15.opExtrude","SWEPT_FACE",FACE,{"disambiguationData":[OSD([sQuery(id+"F13.wireOp",EDGE,"E26.right")])]}),makeQuery(id+"F27.opExtrude","SWEPT_FACE",FACE,{"disambiguationData":[OSD([sQuery(id+"F26.wireOp",EDGE,"E42.left")])]})]});
            var Q14;
            Q14=makeQuery(id+"F27.boolean.opBoolean","INTERSECT",EDGE,{"derivedFrom":[makeQuery(id+"F15.opExtrude","SWEPT_FACE",FACE,{"disambiguationData":[OSD([sQuery(id+"F13.wireOp",EDGE,"E26.top"),sQuery(id+"F13.wireOp",EDGE,"E27.top")])]}),makeQuery(id+"F27.opExtrude","SWEPT_FACE",FACE,{"disambiguationData":[OSD([sQuery(id+"F26.wireOp",EDGE,"E42.left")])]})]});
            var Q15;
            Q15=makeQuery(id+"F27.boolean.opBoolean","INTERSECT",EDGE,{"derivedFrom":[makeQuery(id+"F15.opExtrude","SWEPT_FACE",FACE,{"disambiguationData":[OSD([sQuery(id+"F13.wireOp",EDGE,"E26.right")])]}),makeQuery(id+"F27.opExtrude","SWEPT_FACE",FACE,{"disambiguationData":[OSD([sQuery(id+"F26.wireOp",EDGE,"E42.bottom")])]})]});
            var Q16;
            Q16=makeQuery(id+"F27.boolean.opBoolean","COPY",EDGE,{"derivedFrom":makeQuery(id+"F27.opExtrude","CAP_EDGE",EDGE,{"disambiguationData":[OSD([sQuery(id+"F26.wireOp",EDGE,"E42.bottom")])],"isStart":true})});
            var Q17;
            Q17=makeQuery(id+"F27.boolean.opBoolean","COPY",EDGE,{"derivedFrom":makeQuery(id+"F27.opExtrude","CAP_EDGE",EDGE,{"disambiguationData":[OSD([sQuery(id+"F26.wireOp",EDGE,"E42.left")])],"isStart":true})});
            var Q18;
            Q18=makeQuery(id+"F27.boolean.opBoolean","INTERSECT",EDGE,{"derivedFrom":[makeQuery(id+"F15.opExtrude","SWEPT_FACE",FACE,{"disambiguationData":[OSD([sQuery(id+"F13.wireOp",EDGE,"E26.right")])]}),makeQuery(id+"F27.opExtrude","SWEPT_FACE",FACE,{"disambiguationData":[OSD([sQuery(id+"F26.wireOp",EDGE,"E42.right")])]})]});
            var Q19;
            Q19=makeQuery(id+"F27.boolean.opBoolean","COPY",EDGE,{"derivedFrom":makeQuery(id+"F27.opExtrude","CAP_EDGE",EDGE,{"disambiguationData":[OSD([sQuery(id+"F26.wireOp",EDGE,"E42.right")])],"isStart":true})});
            chamfer(context, id + "F28", {"entities" : qUnion([Q0, Q1, Q2, Q3, Q4, Q5, Q6, Q7, Q8, Q9, Q10, Q11, Q12, Q13, Q14, Q15, Q16, Q17, Q18, Q19]), "width" : .5 * mm, "tangentPropagation" : true});
        }
    });
